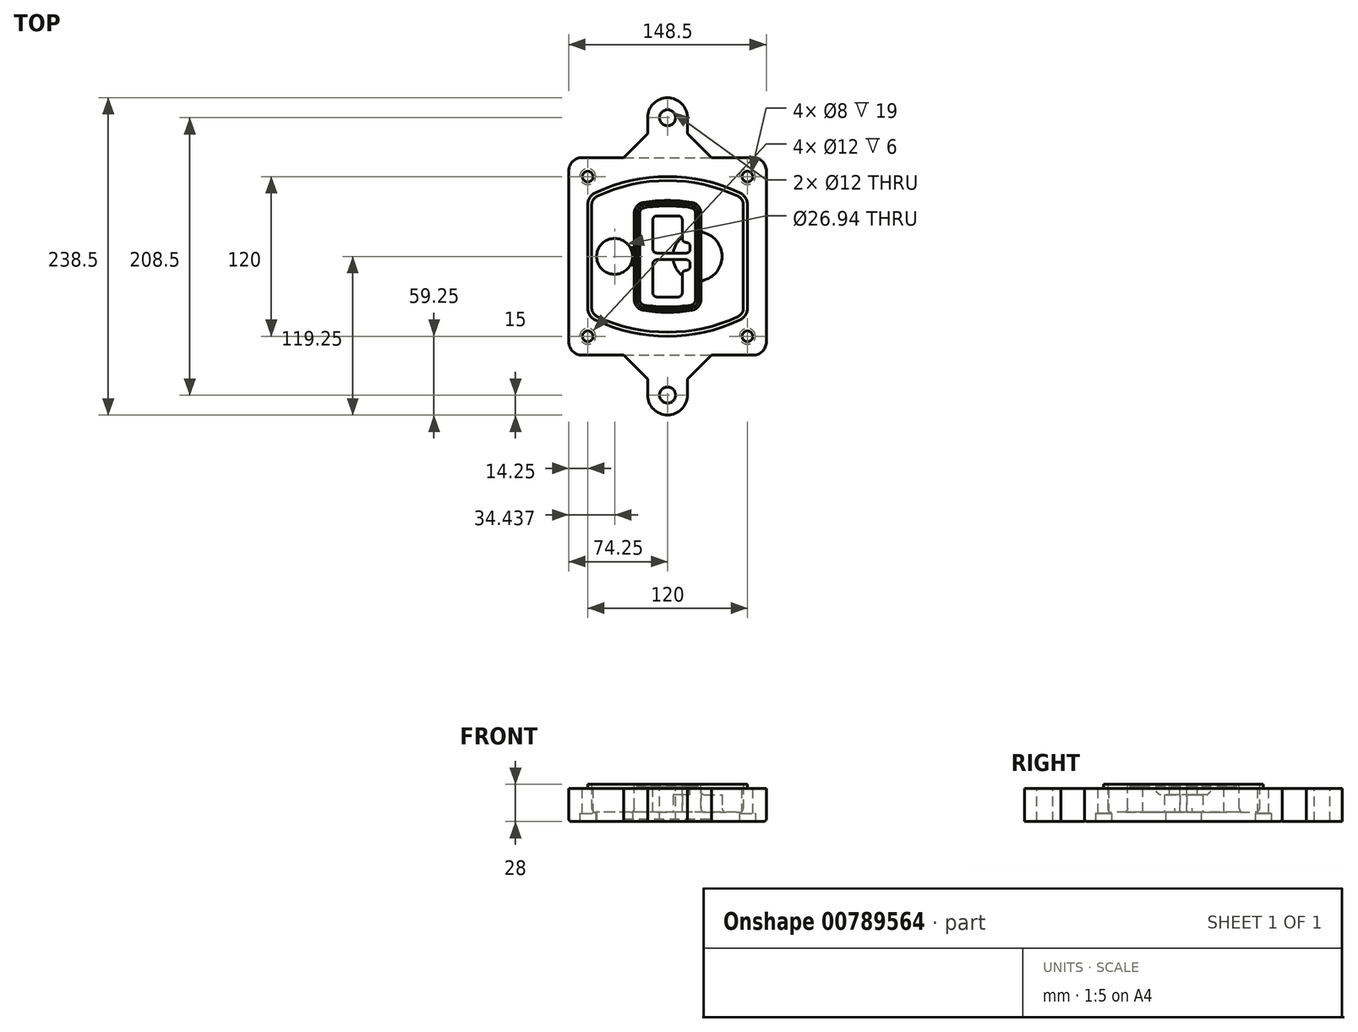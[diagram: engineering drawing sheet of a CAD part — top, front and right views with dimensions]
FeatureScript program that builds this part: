
annotation { "Feature Type Name" : "Feature", "Feature Type Description" : "" }
export const myFeature = defineFeature(function(context is Context, id is Id, definition is map)
    precondition{}
    {
        {
            var Q0;
            Q0=qCreatedBy(makeId("Top.planeOp"),FACE);
            var sketch = newSketch(context, id + "F0", { "sketchPlane" : qUnion([Q0])});
            skPoint(sketch, "E0.rect.middle", {"position": v(0, 0) * mm});
            skLineSegment(sketch, "E1.bottom", {"start": v(-64.25, -74.25) * mm, "end": v(64.25, -74.25) * mm});
            skLineSegment(sketch, "E1.top", {"start": v(-64.25, 74.25) * mm, "end": v(64.25, 74.25) * mm});
            skLineSegment(sketch, "E1.left", {"start": v(-74.25, -64.25) * mm, "end": v(-74.25, 64.25) * mm});
            skLineSegment(sketch, "E1.right", {"start": v(74.25, -64.25) * mm, "end": v(74.25, 64.25) * mm});
            skLineSegment(sketch, "E2", {"start": v(-74.25, 74.25) * mm, "end": v(74.25, -74.25) * mm, "construction": true});
            skLineSegment(sketch, "E3", {"start": v(74.25, 74.25) * mm, "end": v(-74.25, -74.25) * mm, "construction": true});
            skCircle(sketch, "E4", {"center": v(-60, 60) * mm, "radius": 4 * mm});
            skCircle(sketch, "E5", {"center": v(60, 60) * mm, "radius": 4 * mm});
            skCircle(sketch, "E6", {"center": v(60, -60) * mm, "radius": 4 * mm});
            skCircle(sketch, "E7", {"center": v(-60, -60) * mm, "radius": 4 * mm});
            skLineSegment(sketch, "E8", {"start": v(-60, 60) * mm, "end": v(60, 60) * mm, "construction": true});
            skLineSegment(sketch, "E9", {"start": v(60, 60) * mm, "end": v(60, -60) * mm, "construction": true});
            skLineSegment(sketch, "E10", {"start": v(60, -60) * mm, "end": v(-60, -60) * mm, "construction": true});
            skLineSegment(sketch, "E11", {"start": v(-60, -60) * mm, "end": v(-60, 60) * mm, "construction": true});
            skLineSegment(sketch, "E12", {"start": v(-60, 38.83) * mm, "end": v(-60, -38.83) * mm});
            skLineSegment(sketch, "E13", {"start": v(60, 38.83) * mm, "end": v(60, -38.83) * mm});
            skArc(sketch, "E14", {"start": v(54.26, 47.88) * mm, "mid": v(0, 60) * mm, "end": v(-54.26, 47.88) * mm});
            skArc(sketch, "E15", {"start": v(-54.26, -47.88) * mm, "mid": v(0, -60) * mm, "end": v(54.26, -47.88) * mm});
            skLineSegment(sketch, "E16", {"start": v(-60, 0) * mm, "end": v(60, 0) * mm, "construction": true});
            skPoint(sketch, "E17.visualSharp", {"position": v(-60, -45) * mm});
            skArc(sketch, "E17.filletArc", {"start": v(-60, -38.83) * mm, "mid": v(-58.44, -44.2) * mm, "end": v(-54.26, -47.88) * mm});
            skPoint(sketch, "E18.visualSharp", {"position": v(-60, 45) * mm});
            skArc(sketch, "E18.filletArc", {"start": v(-54.26, 47.88) * mm, "mid": v(-58.44, 44.2) * mm, "end": v(-60, 38.83) * mm});
            skPoint(sketch, "E19.visualSharp", {"position": v(60, 45) * mm});
            skArc(sketch, "E19.filletArc", {"start": v(60, 38.83) * mm, "mid": v(58.44, 44.2) * mm, "end": v(54.26, 47.88) * mm});
            skPoint(sketch, "E20.visualSharp", {"position": v(60, -45) * mm});
            skArc(sketch, "E20.filletArc", {"start": v(54.26, -47.88) * mm, "mid": v(58.44, -44.2) * mm, "end": v(60, -38.83) * mm});
            skPoint(sketch, "E21.visualSharp", {"position": v(-74.25, 74.25) * mm});
            skArc(sketch, "E21.filletArc", {"start": v(-64.25, 74.25) * mm, "mid": v(-71.32, 71.32) * mm, "end": v(-74.25, 64.25) * mm});
            skPoint(sketch, "E22.visualSharp", {"position": v(74.25, 74.25) * mm});
            skArc(sketch, "E22.filletArc", {"start": v(74.25, 64.25) * mm, "mid": v(71.32, 71.32) * mm, "end": v(64.25, 74.25) * mm});
            skPoint(sketch, "E23.visualSharp", {"position": v(74.25, -74.25) * mm});
            skArc(sketch, "E23.filletArc", {"start": v(64.25, -74.25) * mm, "mid": v(71.32, -71.32) * mm, "end": v(74.25, -64.25) * mm});
            skPoint(sketch, "E24.visualSharp", {"position": v(-74.25, -74.25) * mm});
            skArc(sketch, "E24.filletArc", {"start": v(-74.25, -64.25) * mm, "mid": v(-71.32, -71.32) * mm, "end": v(-64.25, -74.25) * mm});
            skArc(sketch, "E25.0", {"start": v(57, 38.83) * mm, "mid": v(55.9, 42.58) * mm, "end": v(52.98, 45.17) * mm});
            skLineSegment(sketch, "E25.1", {"start": v(57, 38.83) * mm, "end": v(57, -38.83) * mm});
            skArc(sketch, "E25.2", {"start": v(52.98, -45.17) * mm, "mid": v(55.9, -42.58) * mm, "end": v(57, -38.83) * mm});
            skArc(sketch, "E25.3", {"start": v(-52.98, -45.17) * mm, "mid": v(0, -57) * mm, "end": v(52.98, -45.17) * mm});
            skArc(sketch, "E25.4", {"start": v(-57, -38.83) * mm, "mid": v(-55.9, -42.58) * mm, "end": v(-52.98, -45.17) * mm});
            skArc(sketch, "E25.5", {"start": v(52.98, 45.17) * mm, "mid": v(0, 57) * mm, "end": v(-52.98, 45.17) * mm});
            skLineSegment(sketch, "E25.6", {"start": v(-57, 38.83) * mm, "end": v(-57, -38.83) * mm});
            skArc(sketch, "E25.7", {"start": v(-52.98, 45.17) * mm, "mid": v(-55.9, 42.58) * mm, "end": v(-57, 38.83) * mm});
            skArc(sketch, "E26.0", {"start": v(-55.96, 51.5) * mm, "mid": v(-61.82, 46.33) * mm, "end": v(-64, 38.83) * mm});
            skArc(sketch, "E26.1", {"start": v(55.96, 51.5) * mm, "mid": v(0, 64) * mm, "end": v(-55.96, 51.5) * mm});
            skArc(sketch, "E26.2", {"start": v(64, 38.83) * mm, "mid": v(61.82, 46.33) * mm, "end": v(55.96, 51.5) * mm});
            skLineSegment(sketch, "E26.3", {"start": v(64, 38.83) * mm, "end": v(64, -38.83) * mm});
            skArc(sketch, "E26.4", {"start": v(55.96, -51.5) * mm, "mid": v(61.82, -46.33) * mm, "end": v(64, -38.83) * mm});
            skLineSegment(sketch, "E26.5", {"start": v(-64, 38.83) * mm, "end": v(-64, -38.83) * mm});
            skArc(sketch, "E26.6", {"start": v(-55.96, -51.5) * mm, "mid": v(0, -64) * mm, "end": v(55.96, -51.5) * mm});
            skArc(sketch, "E26.7", {"start": v(-64, -38.83) * mm, "mid": v(-61.82, -46.33) * mm, "end": v(-55.96, -51.5) * mm});
            skSolve(sketch);
        }
        {
            var Q0;
            Q0=makeQuery(id+"F0.imprint","IMPRINT",FACE,{"disambiguationData":[TD([[makeQuery(id+"F0.imprint","IMPRINT",EDGE,{"derivedFrom":sQuery(id+"F0.wireOp",EDGE,"E1.bottom")}),1.0]])]});
            var Q1;
            Q1=makeQuery(id+"F0.imprint","IMPRINT",FACE,{"disambiguationData":[TD([[makeQuery(id+"F0.imprint","IMPRINT",EDGE,{"derivedFrom":sQuery(id+"F0.wireOp",EDGE,"E12")}),1.0]])]});
            var Q2;
            Q2=makeQuery(id+"F0.imprint","IMPRINT",FACE,{"disambiguationData":[TD([[makeQuery(id+"F0.imprint","IMPRINT",EDGE,{"derivedFrom":sQuery(id+"F0.wireOp",EDGE,"E25.0")}),1.0]])]});
            var Q3;
            Q3=makeQuery(id+"F0.imprint","IMPRINT",FACE,{"disambiguationData":[TD([[makeQuery(id+"F0.imprint","IMPRINT",EDGE,{"derivedFrom":sQuery(id+"F0.wireOp",EDGE,"E12")}),-1.0]])]});
            extrude(context, id + "F1", {"entities" : qUnion([Q0, Q1, Q2, Q3]), "oppositeDirection" : true, "depth" : 25 * mm});
        }
        {
            var Q0;
            Q0=makeQuery(id+"F0.imprint","IMPRINT",FACE,{"disambiguationData":[TD([[makeQuery(id+"F0.imprint","IMPRINT",EDGE,{"derivedFrom":sQuery(id+"F0.wireOp",EDGE,"E12")}),1.0]])]});
            extrude(context, id + "F2", {"entities" : qUnion([Q0]), "operationType" : NewBodyOperationType.ADD, "depth" : 3 * mm});
        }
        {
            var Q0;
            Q0=makeQuery(id+"F0.imprint","IMPRINT",FACE,{"disambiguationData":[TD([[makeQuery(id+"F0.imprint","IMPRINT",EDGE,{"derivedFrom":sQuery(id+"F0.wireOp",EDGE,"E25.0")}),1.0]])]});
            extrude(context, id + "F3", {"entities" : qUnion([Q0]), "operationType" : NewBodyOperationType.REMOVE, "oppositeDirection" : true, "depth" : 18 * mm});
        }
        {
            var Q0;
            Q0=makeQuery(id+"F2.opExtrude","CAP_FACE",FACE,{"disambiguationData":[OSD([sQuery(id+"F0.wireOp",EDGE,"E12"),sQuery(id+"F0.wireOp",EDGE,"E13"),sQuery(id+"F0.wireOp",EDGE,"E14"),sQuery(id+"F0.wireOp",EDGE,"E15"),sQuery(id+"F0.wireOp",EDGE,"E17.filletArc"),sQuery(id+"F0.wireOp",EDGE,"E18.filletArc"),sQuery(id+"F0.wireOp",EDGE,"E19.filletArc"),sQuery(id+"F0.wireOp",EDGE,"E20.filletArc"),sQuery(id+"F0.wireOp",EDGE,"E25.0"),sQuery(id+"F0.wireOp",EDGE,"E25.1"),sQuery(id+"F0.wireOp",EDGE,"E25.2"),sQuery(id+"F0.wireOp",EDGE,"E25.3"),sQuery(id+"F0.wireOp",EDGE,"E25.4"),sQuery(id+"F0.wireOp",EDGE,"E25.5"),sQuery(id+"F0.wireOp",EDGE,"E25.6"),sQuery(id+"F0.wireOp",EDGE,"E25.7")])],"isStart":false});
            var sketch = newSketch(context, id + "F4", { "sketchPlane" : qUnion([Q0])});
            skArc(sketch, "E27.0", {"start": v(-18.34, -40.45) * mm, "mid": v(0, -42) * mm, "end": v(18.34, -40.45) * mm});
            skArc(sketch, "E28.0", {"start": v(18.34, 40.45) * mm, "mid": v(0, 42) * mm, "end": v(-18.34, 40.45) * mm});
            skLineSegment(sketch, "E29", {"start": v(-25, 32.57) * mm, "end": v(-25, -32.57) * mm});
            skLineSegment(sketch, "E30", {"start": v(25, 32.57) * mm, "end": v(25, -32.57) * mm});
            skLineSegment(sketch, "E31", {"start": v(-25, 39.1) * mm, "end": v(25, 39.1) * mm, "construction": true});
            skLineSegment(sketch, "E32", {"start": v(-25, -39.1) * mm, "end": v(25, -39.1) * mm, "construction": true});
            skPoint(sketch, "E33.visualSharp", {"position": v(-25, 39.1) * mm});
            skArc(sketch, "E33.filletArc", {"start": v(-18.34, 40.45) * mm, "mid": v(-23.11, 37.73) * mm, "end": v(-25, 32.57) * mm});
            skPoint(sketch, "E34.visualSharp", {"position": v(25, 39.1) * mm});
            skArc(sketch, "E34.filletArc", {"start": v(25, 32.57) * mm, "mid": v(23.11, 37.73) * mm, "end": v(18.34, 40.45) * mm});
            skPoint(sketch, "E35.visualSharp", {"position": v(25, -39.1) * mm});
            skArc(sketch, "E35.filletArc", {"start": v(18.34, -40.45) * mm, "mid": v(23.11, -37.73) * mm, "end": v(25, -32.57) * mm});
            skPoint(sketch, "E36.visualSharp", {"position": v(-25, -39.1) * mm});
            skArc(sketch, "E36.filletArc", {"start": v(-25, -32.57) * mm, "mid": v(-23.11, -37.73) * mm, "end": v(-18.34, -40.45) * mm});
            skArc(sketch, "E37.0", {"start": v(52.98, 45.17) * mm, "mid": v(0, 57) * mm, "end": v(-52.98, 45.17) * mm});
            skArc(sketch, "E37.1", {"start": v(-52.98, 45.17) * mm, "mid": v(-55.9, 42.58) * mm, "end": v(-57, 38.83) * mm});
            skLineSegment(sketch, "E37.2", {"start": v(-57, 38.83) * mm, "end": v(-57, -38.83) * mm});
            skArc(sketch, "E37.3", {"start": v(-57, -38.83) * mm, "mid": v(-55.9, -42.58) * mm, "end": v(-52.98, -45.17) * mm});
            skArc(sketch, "E37.4", {"start": v(-52.98, -45.17) * mm, "mid": v(0, -57) * mm, "end": v(52.98, -45.17) * mm});
            skArc(sketch, "E37.5", {"start": v(52.98, -45.17) * mm, "mid": v(55.9, -42.58) * mm, "end": v(57, -38.83) * mm});
            skLineSegment(sketch, "E37.6", {"start": v(57, 38.83) * mm, "end": v(57, -38.83) * mm});
            skArc(sketch, "E37.7", {"start": v(57, 38.83) * mm, "mid": v(55.9, 42.58) * mm, "end": v(52.98, 45.17) * mm});
            skLineSegment(sketch, "E38.0", {"start": v(23, 32.57) * mm, "end": v(23, -32.57) * mm});
            skArc(sketch, "E38.1", {"start": v(18, -38.48) * mm, "mid": v(21.58, -36.44) * mm, "end": v(23, -32.57) * mm});
            skArc(sketch, "E38.2", {"start": v(-18, -38.48) * mm, "mid": v(0, -40) * mm, "end": v(18, -38.48) * mm});
            skArc(sketch, "E38.3", {"start": v(-23, -32.57) * mm, "mid": v(-21.58, -36.44) * mm, "end": v(-18, -38.48) * mm});
            skLineSegment(sketch, "E38.4", {"start": v(-23, 32.57) * mm, "end": v(-23, -32.57) * mm});
            skArc(sketch, "E38.5", {"start": v(23, 32.57) * mm, "mid": v(21.58, 36.44) * mm, "end": v(18, 38.48) * mm});
            skArc(sketch, "E38.6", {"start": v(-18, 38.48) * mm, "mid": v(-21.58, 36.44) * mm, "end": v(-23, 32.57) * mm});
            skArc(sketch, "E38.7", {"start": v(18, 38.48) * mm, "mid": v(0, 40) * mm, "end": v(-18, 38.48) * mm});
            skArc(sketch, "E39.0", {"start": v(21, 32.57) * mm, "mid": v(20.06, 35.15) * mm, "end": v(17.67, 36.5) * mm});
            skLineSegment(sketch, "E39.1", {"start": v(21, 32.57) * mm, "end": v(21, -32.57) * mm});
            skArc(sketch, "E39.2", {"start": v(17.67, -36.5) * mm, "mid": v(20.06, -35.15) * mm, "end": v(21, -32.57) * mm});
            skArc(sketch, "E39.3", {"start": v(-17.67, -36.5) * mm, "mid": v(0, -38) * mm, "end": v(17.67, -36.5) * mm});
            skArc(sketch, "E39.4", {"start": v(-21, -32.57) * mm, "mid": v(-20.06, -35.15) * mm, "end": v(-17.67, -36.5) * mm});
            skArc(sketch, "E39.5", {"start": v(17.67, 36.5) * mm, "mid": v(0, 38) * mm, "end": v(-17.67, 36.5) * mm});
            skLineSegment(sketch, "E39.6", {"start": v(-21, 32.57) * mm, "end": v(-21, -32.57) * mm});
            skArc(sketch, "E39.7", {"start": v(-17.67, 36.5) * mm, "mid": v(-20.06, 35.15) * mm, "end": v(-21, 32.57) * mm});
            skLineSegment(sketch, "E40", {"start": v(-25, 0) * mm, "end": v(25, 0) * mm, "construction": true});
            skLineSegment(sketch, "E41", {"start": v(-11, 5.5) * mm, "end": v(-11, 27.5) * mm});
            skLineSegment(sketch, "E42", {"start": v(-8, 30.5) * mm, "end": v(8, 30.5) * mm});
            skLineSegment(sketch, "E43", {"start": v(11, 27.5) * mm, "end": v(11, 13.5) * mm});
            skLineSegment(sketch, "E44", {"start": v(14, 10.5) * mm, "end": v(14, 10.5) * mm});
            skLineSegment(sketch, "E45", {"start": v(17, 7.5) * mm, "end": v(17, 5.5) * mm});
            skLineSegment(sketch, "E46", {"start": v(14, 2.5) * mm, "end": v(-8, 2.5) * mm});
            skPoint(sketch, "E47.visualSharp", {"position": v(-11, 30.5) * mm});
            skArc(sketch, "E47.filletArc", {"start": v(-8, 30.5) * mm, "mid": v(-10.12, 29.62) * mm, "end": v(-11, 27.5) * mm});
            skPoint(sketch, "E48.visualSharp", {"position": v(11, 30.5) * mm});
            skArc(sketch, "E48.filletArc", {"start": v(11, 27.5) * mm, "mid": v(10.12, 29.62) * mm, "end": v(8, 30.5) * mm});
            skPoint(sketch, "E49.visualSharp", {"position": v(11, 10.5) * mm});
            skArc(sketch, "E49.filletArc", {"start": v(11, 13.5) * mm, "mid": v(11.88, 11.38) * mm, "end": v(14, 10.5) * mm});
            skPoint(sketch, "E50.visualSharp", {"position": v(17, 10.5) * mm});
            skArc(sketch, "E50.filletArc", {"start": v(17, 7.5) * mm, "mid": v(16.12, 9.62) * mm, "end": v(14, 10.5) * mm});
            skPoint(sketch, "E51.visualSharp", {"position": v(17, 2.5) * mm});
            skArc(sketch, "E51.filletArc", {"start": v(14, 2.5) * mm, "mid": v(16.12, 3.38) * mm, "end": v(17, 5.5) * mm});
            skPoint(sketch, "E52.visualSharp", {"position": v(-11, 2.5) * mm});
            skArc(sketch, "E52.filletArc", {"start": v(-11, 5.5) * mm, "mid": v(-10.12, 3.38) * mm, "end": v(-8, 2.5) * mm});
            skLineSegment(sketch, "E53.0.MirrorCS", {"start": v(14, -2.5) * mm, "end": v(-8, -2.5) * mm});
            skArc(sketch, "E54.0.MirrorCS", {"start": v(-11, -5.5) * mm, "mid": v(-10.12, -3.38) * mm, "end": v(-8, -2.5) * mm});
            skLineSegment(sketch, "E55.0.MirrorCS", {"start": v(-11, -5.5) * mm, "end": v(-11, -27.5) * mm});
            skArc(sketch, "E56.0.MirrorCS", {"start": v(-8, -30.5) * mm, "mid": v(-10.12, -29.62) * mm, "end": v(-11, -27.5) * mm});
            skLineSegment(sketch, "E57.0.MirrorCS", {"start": v(-8, -30.5) * mm, "end": v(8, -30.5) * mm});
            skArc(sketch, "E58.0.MirrorCS", {"start": v(11, -27.5) * mm, "mid": v(10.12, -29.62) * mm, "end": v(8, -30.5) * mm});
            skLineSegment(sketch, "E59.0.MirrorCS", {"start": v(11, -27.5) * mm, "end": v(11, -13.5) * mm});
            skArc(sketch, "E60.0.MirrorCS", {"start": v(11, -13.5) * mm, "mid": v(11.88, -11.38) * mm, "end": v(14, -10.5) * mm});
            skArc(sketch, "E61.0.MirrorCS", {"start": v(17, -7.5) * mm, "mid": v(16.12, -9.62) * mm, "end": v(14, -10.5) * mm});
            skLineSegment(sketch, "E62.0.MirrorCS", {"start": v(17, -7.5) * mm, "end": v(17, -5.5) * mm});
            skArc(sketch, "E63.0.MirrorCS", {"start": v(14, -2.5) * mm, "mid": v(16.12, -3.38) * mm, "end": v(17, -5.5) * mm});
            skSolve(sketch);
        }
        {
            var Q0;
            Q0=makeQuery(id+"F4.imprint","IMPRINT",FACE,{"disambiguationData":[TD([[makeQuery(id+"F4.imprint","IMPRINT",EDGE,{"derivedFrom":sQuery(id+"F4.wireOp",EDGE,"E27.0")}),1.0]])]});
            var Q1;
            Q1=makeQuery(id+"F4.imprint","IMPRINT",FACE,{"disambiguationData":[TD([[makeQuery(id+"F4.imprint","IMPRINT",EDGE,{"derivedFrom":sQuery(id+"F4.wireOp",EDGE,"E38.0")}),-1.0]])]});
            var Q2;
            Q2=makeQuery(id+"F4.imprint","IMPRINT",FACE,{"disambiguationData":[TD([[makeQuery(id+"F4.imprint","IMPRINT",EDGE,{"derivedFrom":sQuery(id+"F4.wireOp",EDGE,"E39.0")}),1.0]])]});
            extrude(context, id + "F5", {"entities" : qUnion([Q0, Q1, Q2]), "operationType" : NewBodyOperationType.ADD, "endBound" : BoundingType.UP_TO_NEXT, "oppositeDirection" : true, "depth" : 25 * mm});
        }
        {
            var Q0;
            Q0=makeQuery(id+"F4.imprint","IMPRINT",FACE,{"disambiguationData":[TD([[makeQuery(id+"F4.imprint","IMPRINT",EDGE,{"derivedFrom":sQuery(id+"F4.wireOp",EDGE,"E38.0")}),-1.0]])]});
            extrude(context, id + "F6", {"entities" : qUnion([Q0]), "operationType" : NewBodyOperationType.REMOVE, "oppositeDirection" : true, "depth" : 2 * mm});
        }
        {
            var Q0;
            Q0=makeQuery(id+"F1.opExtrude","CAP_FACE",FACE,{"disambiguationData":[OSD([sQuery(id+"F0.wireOp",EDGE,"E1.bottom"),sQuery(id+"F0.wireOp",EDGE,"E1.top"),sQuery(id+"F0.wireOp",EDGE,"E1.left"),sQuery(id+"F0.wireOp",EDGE,"E1.right"),sQuery(id+"F0.wireOp",EDGE,"E4"),sQuery(id+"F0.wireOp",EDGE,"E5"),sQuery(id+"F0.wireOp",EDGE,"E6"),sQuery(id+"F0.wireOp",EDGE,"E7"),sQuery(id+"F0.wireOp",EDGE,"E21.filletArc"),sQuery(id+"F0.wireOp",EDGE,"E22.filletArc"),sQuery(id+"F0.wireOp",EDGE,"E23.filletArc"),sQuery(id+"F0.wireOp",EDGE,"E24.filletArc")])],"isStart":false});
            var sketch = newSketch(context, id + "F7", { "sketchPlane" : qUnion([Q0])});
            skCircle(sketch, "E64", {"center": v(22.5, 0) * mm, "radius": 13.47 * mm});
            skCircle(sketch, "E65", {"center": v(-39.81, 0) * mm, "radius": 13.47 * mm});
            skLineSegment(sketch, "E66", {"start": v(74.25, 0) * mm, "end": v(-74.25, 0) * mm});
            skCircle(sketch, "E67", {"center": v(22.5, 0) * mm, "radius": 18.47 * mm});
            skCircle(sketch, "E68", {"center": v(60, -60) * mm, "radius": 6 * mm});
            skCircle(sketch, "E69", {"center": v(-60, -60) * mm, "radius": 6 * mm});
            skCircle(sketch, "E70", {"center": v(-60, 60) * mm, "radius": 6 * mm});
            skCircle(sketch, "E71", {"center": v(60, 60) * mm, "radius": 6 * mm});
            skSolve(sketch);
        }
        {
            var Q0;
            {var subQ1=sQuery(id+"F7.wireOp",EDGE,"E66");var subQ4=sQuery(id+"F7.wireOp",EDGE,"E64");var subQ6=makeQuery(id+"F7.imprint","INTERSECT",VERTEX,{"disambiguationData":[OD(0.0)],"derivedFrom":[subQ4,subQ1]});Q0=makeQuery(id+"F7.imprint","IMPRINT",FACE,{"disambiguationData":[TD([[makeQuery(id+"F7.imprint","IMPRINT",EDGE,{"disambiguationData":[TD([[subQ6,-1.0]])],"derivedFrom":subQ4}),-1.0]])]});}
            var Q1;
            {var subQ0=sQuery(id+"F7.wireOp",EDGE,"E66");var subQ1=sQuery(id+"F7.wireOp",EDGE,"E64");var subQ3=makeQuery(id+"F7.imprint","INTERSECT",VERTEX,{"disambiguationData":[OD(0.0)],"derivedFrom":[subQ1,subQ0]});Q1=makeQuery(id+"F7.imprint","IMPRINT",FACE,{"disambiguationData":[TD([[makeQuery(id+"F7.imprint","IMPRINT",EDGE,{"disambiguationData":[TD([[subQ3,-1.0]])],"derivedFrom":subQ1}),1.0]])]});}
            var Q2;
            {var subQ0=sQuery(id+"F7.wireOp",EDGE,"E66");var subQ1=sQuery(id+"F7.wireOp",EDGE,"E64");var subQ3=makeQuery(id+"F7.imprint","INTERSECT",VERTEX,{"disambiguationData":[OD(0.0)],"derivedFrom":[subQ1,subQ0]});Q2=makeQuery(id+"F7.imprint","IMPRINT",FACE,{"disambiguationData":[TD([[makeQuery(id+"F7.imprint","IMPRINT",EDGE,{"disambiguationData":[TD([[subQ3,1.0]])],"derivedFrom":subQ1}),1.0]])]});}
            var Q3;
            {var subQ1=sQuery(id+"F7.wireOp",EDGE,"E66");var subQ4=sQuery(id+"F7.wireOp",EDGE,"E64");var subQ6=makeQuery(id+"F7.imprint","INTERSECT",VERTEX,{"disambiguationData":[OD(0.0)],"derivedFrom":[subQ4,subQ1]});Q3=makeQuery(id+"F7.imprint","IMPRINT",FACE,{"disambiguationData":[TD([[makeQuery(id+"F7.imprint","IMPRINT",EDGE,{"disambiguationData":[TD([[subQ6,1.0]])],"derivedFrom":subQ4}),-1.0]])]});}
            extrude(context, id + "F8", {"entities" : qUnion([Q0, Q1, Q2, Q3]), "operationType" : NewBodyOperationType.ADD, "oppositeDirection" : true, "depth" : 20 * mm});
        }
        {
            var Q0;
            {var subQ0=sQuery(id+"F7.wireOp",EDGE,"E66");var subQ1=sQuery(id+"F7.wireOp",EDGE,"E65");var subQ3=makeQuery(id+"F7.imprint","INTERSECT",VERTEX,{"disambiguationData":[OD(0.0)],"derivedFrom":[subQ1,subQ0]});Q0=makeQuery(id+"F7.imprint","IMPRINT",FACE,{"disambiguationData":[TD([[makeQuery(id+"F7.imprint","IMPRINT",EDGE,{"disambiguationData":[TD([[subQ3,-1.0]])],"derivedFrom":subQ1}),1.0]])]});}
            var Q1;
            {var subQ0=sQuery(id+"F7.wireOp",EDGE,"E66");var subQ1=sQuery(id+"F7.wireOp",EDGE,"E65");var subQ3=makeQuery(id+"F7.imprint","INTERSECT",VERTEX,{"disambiguationData":[OD(0.0)],"derivedFrom":[subQ1,subQ0]});Q1=makeQuery(id+"F7.imprint","IMPRINT",FACE,{"disambiguationData":[TD([[makeQuery(id+"F7.imprint","IMPRINT",EDGE,{"disambiguationData":[TD([[subQ3,1.0]])],"derivedFrom":subQ1}),1.0]])]});}
            extrude(context, id + "F9", {"entities" : qUnion([Q0, Q1]), "operationType" : NewBodyOperationType.REMOVE, "oppositeDirection" : true, "depth" : 25 * mm});
        }
        {
            var Q0;
            Q0=makeQuery(id+"F7.imprint","IMPRINT",FACE,{"disambiguationData":[TD([[makeQuery(id+"F7.imprint","IMPRINT",EDGE,{"derivedFrom":sQuery(id+"F7.wireOp",EDGE,"E68")}),1.0]])]});
            var Q1;
            Q1=makeQuery(id+"F7.imprint","IMPRINT",FACE,{"disambiguationData":[TD([[makeQuery(id+"F7.imprint","IMPRINT",EDGE,{"derivedFrom":makeQuery(id+"F1.opExtrude","CAP_EDGE",EDGE,{"disambiguationData":[OSD([sQuery(id+"F0.wireOp",EDGE,"E5")])],"isStart":false})}),-1.0]])]});
            var Q2;
            Q2=makeQuery(id+"F7.imprint","IMPRINT",FACE,{"disambiguationData":[TD([[makeQuery(id+"F7.imprint","IMPRINT",EDGE,{"derivedFrom":sQuery(id+"F7.wireOp",EDGE,"E69")}),1.0]])]});
            var Q3;
            Q3=makeQuery(id+"F7.imprint","IMPRINT",FACE,{"disambiguationData":[TD([[makeQuery(id+"F7.imprint","IMPRINT",EDGE,{"derivedFrom":makeQuery(id+"F1.opExtrude","CAP_EDGE",EDGE,{"disambiguationData":[OSD([sQuery(id+"F0.wireOp",EDGE,"E4")])],"isStart":false})}),-1.0]])]});
            var Q4;
            Q4=makeQuery(id+"F7.imprint","IMPRINT",FACE,{"disambiguationData":[TD([[makeQuery(id+"F7.imprint","IMPRINT",EDGE,{"derivedFrom":sQuery(id+"F7.wireOp",EDGE,"E70")}),1.0]])]});
            var Q5;
            Q5=makeQuery(id+"F7.imprint","IMPRINT",FACE,{"disambiguationData":[TD([[makeQuery(id+"F7.imprint","IMPRINT",EDGE,{"derivedFrom":makeQuery(id+"F1.opExtrude","CAP_EDGE",EDGE,{"disambiguationData":[OSD([sQuery(id+"F0.wireOp",EDGE,"E7")])],"isStart":false})}),-1.0]])]});
            var Q6;
            Q6=makeQuery(id+"F7.imprint","IMPRINT",FACE,{"disambiguationData":[TD([[makeQuery(id+"F7.imprint","IMPRINT",EDGE,{"derivedFrom":sQuery(id+"F7.wireOp",EDGE,"E71")}),1.0]])]});
            var Q7;
            Q7=makeQuery(id+"F7.imprint","IMPRINT",FACE,{"disambiguationData":[TD([[makeQuery(id+"F7.imprint","IMPRINT",EDGE,{"derivedFrom":makeQuery(id+"F1.opExtrude","CAP_EDGE",EDGE,{"disambiguationData":[OSD([sQuery(id+"F0.wireOp",EDGE,"E6")])],"isStart":false})}),-1.0]])]});
            extrude(context, id + "F10", {"entities" : qUnion([Q0, Q1, Q2, Q3, Q4, Q5, Q6, Q7]), "operationType" : NewBodyOperationType.REMOVE, "oppositeDirection" : true, "depth" : 6 * mm});
        }
        {
            var Q0;
            Q0=makeQuery(id+"F3.boolean.opBoolean","COPY",EDGE,{"derivedFrom":makeQuery(id+"F3.opExtrude","CAP_EDGE",EDGE,{"disambiguationData":[OSD([sQuery(id+"F0.wireOp",EDGE,"E25.6")])],"isStart":false})});
            var Q1;
            Q1=makeQuery(id+"F8.boolean.opBoolean","INTERSECT",EDGE,{"derivedFrom":[makeQuery(id+"F5.opExtrude","SWEPT_FACE",FACE,{"disambiguationData":[OSD([sQuery(id+"F4.wireOp",EDGE,"E30")])]}),makeQuery(id+"F8.opExtrude","CAP_FACE",FACE,{"disambiguationData":[OSD([sQuery(id+"F7.wireOp",EDGE,"E67")])],"isStart":false})]});
            var Q2;
            Q2=makeQuery(id+"F8.boolean.opBoolean","INTERSECT",EDGE,{"disambiguationData":[OD(1.0)],"derivedFrom":[makeQuery(id+"F5.opExtrude","SWEPT_FACE",FACE,{"disambiguationData":[OSD([sQuery(id+"F4.wireOp",EDGE,"E30")])]}),makeQuery(id+"F8.opExtrude","SWEPT_FACE",FACE,{"disambiguationData":[OSD([sQuery(id+"F7.wireOp",EDGE,"E67")])]})]});
            var Q3;
            {var subQ0=sQuery(id+"F4.wireOp",EDGE,"E30");Q3=makeQuery(id+"F8.boolean.opBoolean","SPLIT",EDGE,{"disambiguationData":[TD([makeQuery(id+"F5.opExtrude","SWEPT_FACE",FACE,{"disambiguationData":[OSD([sQuery(id+"F4.wireOp",EDGE,"E35.filletArc")])]})])],"derivedFrom":makeQuery(id+"F5.opExtrude","CAP_EDGE",EDGE,{"disambiguationData":[OSD([subQ0])],"isStart":false})});}
            var Q4;
            {var subQ0=sQuery(id+"F0.wireOp",EDGE,"E25.7");var subQ1=sQuery(id+"F0.wireOp",EDGE,"E25.1");var subQ2=sQuery(id+"F0.wireOp",EDGE,"E25.6");var subQ3=sQuery(id+"F0.wireOp",EDGE,"E25.5");var subQ4=sQuery(id+"F0.wireOp",EDGE,"E25.4");var subQ5=sQuery(id+"F0.wireOp",EDGE,"E25.0");var subQ6=sQuery(id+"F0.wireOp",EDGE,"E25.2");var subQ7=sQuery(id+"F0.wireOp",EDGE,"E25.3");Q4=makeQuery(id+"F8.boolean.opBoolean","INTERSECT",EDGE,{"derivedFrom":[makeQuery(id+"F5.boolean.opBoolean","SPLIT",FACE,{"disambiguationData":[TD([makeQuery(id+"F2.opExtrude","SWEPT_FACE",FACE,{"disambiguationData":[OSD([subQ5])]})])],"derivedFrom":makeQuery(id+"F3.boolean.opBoolean","COPY",FACE,{"derivedFrom":makeQuery(id+"F3.opExtrude","CAP_FACE",FACE,{"disambiguationData":[OSD([subQ5,subQ1,subQ6,subQ7,subQ4,subQ3,subQ2,subQ0])],"isStart":false})})}),makeQuery(id+"F8.opExtrude","SWEPT_FACE",FACE,{"disambiguationData":[OSD([sQuery(id+"F7.wireOp",EDGE,"E67")])]})]});}
            var Q5;
            Q5=makeQuery(id+"F8.boolean.opBoolean","INTERSECT",EDGE,{"disambiguationData":[OD(0.0)],"derivedFrom":[makeQuery(id+"F5.opExtrude","SWEPT_FACE",FACE,{"disambiguationData":[OSD([sQuery(id+"F4.wireOp",EDGE,"E30")])]}),makeQuery(id+"F8.opExtrude","SWEPT_FACE",FACE,{"disambiguationData":[OSD([sQuery(id+"F7.wireOp",EDGE,"E67")])]})]});
            fillet(context, id + "F11", {"entities" : qUnion([Q0, Q1, Q2, Q3, Q4, Q5]), "radius" : 3 * mm, "tangentPropagation" : true, "allowEdgeOverflow" : false});
        }
        {
            var Q0;
            Q0=makeQuery(id+"F1.opExtrude","CAP_EDGE",EDGE,{"disambiguationData":[OSD([sQuery(id+"F0.wireOp",EDGE,"E1.bottom")])],"isStart":false});
            fillet(context, id + "F12", {"entities" : qUnion([Q0]), "radius" : 2 * mm, "tangentPropagation" : true, "allowEdgeOverflow" : false});
        }
        {
            var Q0;
            {var subQ0=sQuery(id+"F0.wireOp",EDGE,"E21.filletArc");var subQ1=sQuery(id+"F0.wireOp",EDGE,"E7");var subQ2=sQuery(id+"F0.wireOp",EDGE,"E6");var subQ3=sQuery(id+"F0.wireOp",EDGE,"E5");var subQ4=sQuery(id+"F0.wireOp",EDGE,"E4");var subQ5=sQuery(id+"F0.wireOp",EDGE,"E22.filletArc");var subQ6=sQuery(id+"F0.wireOp",EDGE,"E1.bottom");var subQ7=sQuery(id+"F0.wireOp",EDGE,"E1.right");var subQ8=sQuery(id+"F0.wireOp",EDGE,"E1.top");var subQ9=sQuery(id+"F0.wireOp",EDGE,"E1.left");var subQ10=sQuery(id+"F0.wireOp",EDGE,"E23.filletArc");var subQ11=sQuery(id+"F0.wireOp",EDGE,"E24.filletArc");Q0=makeQuery(id+"F2.boolean.opBoolean","SPLIT",FACE,{"disambiguationData":[TD([makeQuery(id+"F1.opExtrude","SWEPT_FACE",FACE,{"disambiguationData":[OSD([subQ6])]})])],"derivedFrom":makeQuery(id+"F1.opExtrude","CAP_FACE",FACE,{"disambiguationData":[OSD([subQ6,subQ8,subQ9,subQ7,subQ4,subQ3,subQ2,subQ1,subQ0,subQ5,subQ10,subQ11])],"isStart":true})});}
            var sketch = newSketch(context, id + "F13", { "sketchPlane" : qUnion([Q0])});
            skLineSegment(sketch, "E72", {"start": v(-33, 74.25) * mm, "end": v(-15, 92.25) * mm});
            skLineSegment(sketch, "E73", {"start": v(-15, 92.25) * mm, "end": v(-15, 104.25) * mm});
            skArc(sketch, "E74", {"start": v(-15, 104.25) * mm, "mid": v(0, 119.25) * mm, "end": v(15, 104.25) * mm});
            skLineSegment(sketch, "E75", {"start": v(15, 104.25) * mm, "end": v(15, 92.25) * mm});
            skLineSegment(sketch, "E76", {"start": v(15, 92.25) * mm, "end": v(33, 74.25) * mm});
            skCircle(sketch, "E77", {"center": v(0, 104.25) * mm, "radius": 6 * mm});
            skLineSegment(sketch, "E78", {"start": v(-33, 74.25) * mm, "end": v(33, 74.25) * mm});
            skLineSegment(sketch, "E79", {"start": v(0, 138.51) * mm, "end": v(0, 64.25) * mm});
            skPoint(sketch, "E79.endSnap0", {"position": v(0, 74.25) * mm});
            skLineSegment(sketch, "E80", {"start": v(0, -137.4) * mm, "end": v(0, -67.5) * mm});
            skPoint(sketch, "E80.startSnap0", {"position": v(0, -74.25) * mm});
            skLineSegment(sketch, "E81", {"start": v(-99.15, 0) * mm, "end": v(109.3, 0) * mm, "construction": true});
            skPoint(sketch, "E81.startSnap0", {"position": v(-74.25, 0) * mm});
            skLineSegment(sketch, "E82.MirrorCS", {"start": v(-33, -74.25) * mm, "end": v(33, -74.25) * mm});
            skLineSegment(sketch, "E83.MirrorCS", {"start": v(15, -92.25) * mm, "end": v(33, -74.25) * mm});
            skLineSegment(sketch, "E84.MirrorCS", {"start": v(-33, -74.25) * mm, "end": v(-15, -92.25) * mm});
            skLineSegment(sketch, "E85.MirrorCS", {"start": v(15, -104.25) * mm, "end": v(15, -92.25) * mm});
            skLineSegment(sketch, "E86.MirrorCS", {"start": v(-15, -92.25) * mm, "end": v(-15, -104.25) * mm});
            skCircle(sketch, "E87.MirrorC", {"center": v(0, -104.25) * mm, "radius": 6 * mm});
            skArc(sketch, "E88.MirrorCS", {"start": v(-15, -104.25) * mm, "mid": v(0, -119.25) * mm, "end": v(15, -104.25) * mm});
            skSolve(sketch);
        }
        {
            var Q0;
            Q0 = qSketchRegion(id + "F13", true);
            var Q1;
            Q1=makeQuery(id+"F1.opExtrude","CAP_FACE",FACE,{"disambiguationData":[OSD([sQuery(id+"F0.wireOp",EDGE,"E1.bottom"),sQuery(id+"F0.wireOp",EDGE,"E1.top"),sQuery(id+"F0.wireOp",EDGE,"E1.left"),sQuery(id+"F0.wireOp",EDGE,"E1.right"),sQuery(id+"F0.wireOp",EDGE,"E4"),sQuery(id+"F0.wireOp",EDGE,"E5"),sQuery(id+"F0.wireOp",EDGE,"E6"),sQuery(id+"F0.wireOp",EDGE,"E7"),sQuery(id+"F0.wireOp",EDGE,"E21.filletArc"),sQuery(id+"F0.wireOp",EDGE,"E22.filletArc"),sQuery(id+"F0.wireOp",EDGE,"E23.filletArc"),sQuery(id+"F0.wireOp",EDGE,"E24.filletArc")])],"isStart":false});
            extrude(context, id + "F14", {"entities" : qUnion([Q0]), "operationType" : NewBodyOperationType.ADD, "endBound" : BoundingType.UP_TO_SURFACE, "oppositeDirection" : true, "depth" : 25 * mm, "endBoundEntityFace" : qUnion([Q1]), "offsetDistance" : 25 * mm});
        }
    });
